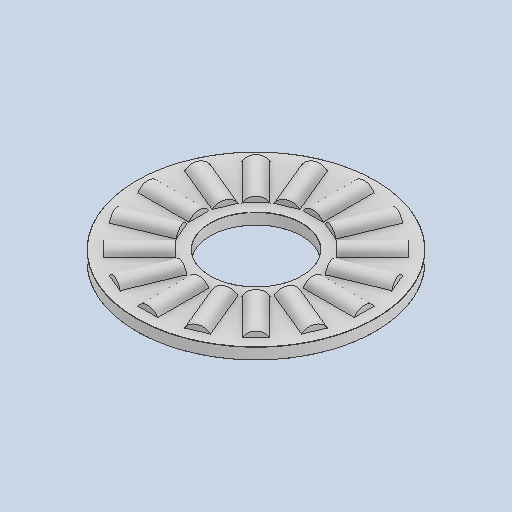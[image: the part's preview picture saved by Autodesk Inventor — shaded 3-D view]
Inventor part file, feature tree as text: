
AUTODESK INVENTOR PART (.ipt)
format: ipt  version: 2023 (Build 270158030, 158C)  size: 296,448 bytes
history: native  units: in
note: dims shown in document units (in); Inventor stores cm internally (conversion verified against a paired STEP export)
features: other x15, revolve x1, pattern_circular x1
ambient origin geometry x8: Origin, YZ Plane, XZ Plane, XY Plane, X Axis, Y Axis, Z Axis, Center Point
bodies: Solid1 (feature_tree), Solid2 (feature_tree), Solid3 (feature_tree), Solid4 (feature_tree), Solid5 (feature_tree), Solid6 (feature_tree), Solid7 (feature_tree), Solid8 (feature_tree), Solid9 (feature_tree), Solid10 (feature_tree), Solid11 (feature_tree), Solid12 (feature_tree), Solid13 (feature_tree), Solid14 (feature_tree), Solid15 (feature_tree), Solid16 (feature_tree), Solid17 (feature_tree)
feature tree (17):
  revolve  "Revolve2"  [1 undecoded]
  pattern_circular  "CirPattern2"
  other  "CirPattern3[1]"
  other  "CirPattern3[2]"
  other  "CirPattern3[3]"
  other  "CirPattern3[4]"
  other  "CirPattern3[5]"
  other  "CirPattern3[6]"
  other  "CirPattern3[7]"
  other  "CirPattern3[8]"
  other  "CirPattern3[9]"
  other  "CirPattern3[10]"
  other  "CirPattern3[11]"
  other  "CirPattern3[12]"
  other  "CirPattern3[13]"
  other  "CirPattern3[14]"
  other  "CirPattern3[15]"
note: 1 required parameter value undecoded (feature->parameter linkage not recoverable at this tier; creation-order binding heuristic only, values carry confidence <= 0.55)
